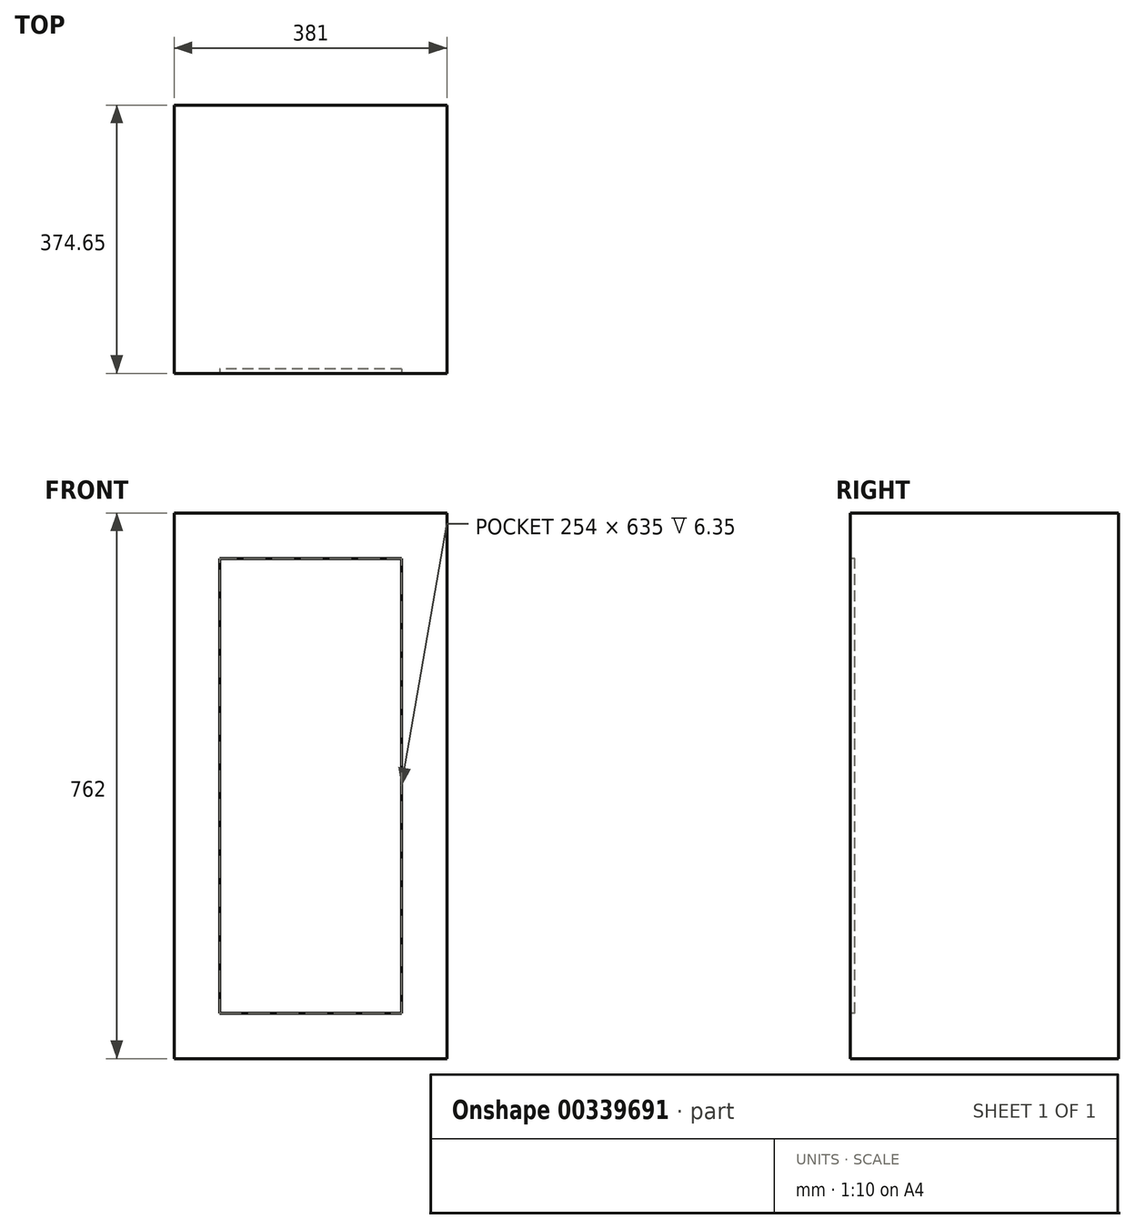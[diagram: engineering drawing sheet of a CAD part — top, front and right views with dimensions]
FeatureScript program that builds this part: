
annotation { "Feature Type Name" : "Feature", "Feature Type Description" : "" }
export const myFeature = defineFeature(function(context is Context, id is Id, definition is map)
    precondition{}
    {
        {
            var Q0;
            Q0=qCreatedBy(makeId("Front.planeOp"),FACE);
            var sketch = newSketch(context, id + "F0", { "sketchPlane" : qUnion([Q0])});
            skLineSegment(sketch, "E0.bottom", {"start": v(263.93, 0) * mm, "end": v(-117.07, 0) * mm});
            skLineSegment(sketch, "E0.top", {"start": v(263.93, 762) * mm, "end": v(-117.07, 762) * mm});
            skLineSegment(sketch, "E0.left", {"start": v(263.93, 0) * mm, "end": v(263.93, 762) * mm});
            skLineSegment(sketch, "E0.right", {"start": v(-117.07, 0) * mm, "end": v(-117.07, 762) * mm});
            skLineSegment(sketch, "E1.0", {"start": v(200.43, 698.5) * mm, "end": v(-53.57, 698.5) * mm});
            skLineSegment(sketch, "E1.1", {"start": v(200.43, 63.5) * mm, "end": v(200.43, 698.5) * mm});
            skLineSegment(sketch, "E1.2", {"start": v(200.43, 63.5) * mm, "end": v(-53.57, 63.5) * mm});
            skLineSegment(sketch, "E1.3", {"start": v(-53.57, 63.5) * mm, "end": v(-53.57, 698.5) * mm});
            skLineSegment(sketch, "E2.bottom", {"start": v(-117.07, 0) * mm, "end": v(263.93, 0) * mm});
            skLineSegment(sketch, "E3.bottom", {"start": v(-117.07, 762) * mm, "end": v(263.93, 762) * mm});
            skSolve(sketch);
        }
        {
            var Q0;
            Q0=makeQuery(id+"F0.imprint","IMPRINT",FACE,{"disambiguationData":[TD([[makeQuery(id+"F0.imprint","IMPRINT",EDGE,{"derivedFrom":sQuery(id+"F0.wireOp",EDGE,"E0.top")}),1.0]])]});
            var Q1;
            Q1=makeQuery(id+"F0.imprint","IMPRINT",FACE,{"disambiguationData":[TD([[makeQuery(id+"F0.imprint","IMPRINT",EDGE,{"derivedFrom":sQuery(id+"F0.wireOp",EDGE,"E1.0")}),1.0]])]});
            var Q2;
            Q2=makeQuery(id+"F0.imprint","IMPRINT",FACE,{"disambiguationData":[TD([[makeQuery(id+"F0.imprint","IMPRINT",EDGE,{"derivedFrom":sQuery(id+"F0.wireOp",EDGE,"E2.bottom")}),-1.0]])]});
            var Q3;
            Q3=makeQuery(id+"F0.imprint","IMPRINT",FACE,{"disambiguationData":[TD([[makeQuery(id+"F0.imprint","IMPRINT",EDGE,{"derivedFrom":sQuery(id+"F0.wireOp",EDGE,"E3.bottom")}),1.0]])]});
            var Q4;
            Q4=makeQuery(id+"F0.imprint","IMPRINT",FACE,{"disambiguationData":[TD([[makeQuery(id+"F0.imprint","IMPRINT",EDGE,{"derivedFrom":sQuery(id+"F0.wireOp",EDGE,"E0.left")}),1.0]])]});
            var Q5;
            Q5=makeQuery(id+"F0.imprint","IMPRINT",FACE,{"disambiguationData":[TD([[makeQuery(id+"F0.imprint","IMPRINT",EDGE,{"derivedFrom":sQuery(id+"F0.wireOp",EDGE,"E3.top")}),-1.0]])]});
            var Q6;
            Q6=makeQuery(id+"F0.imprint","IMPRINT",FACE,{"disambiguationData":[TD([[makeQuery(id+"F0.imprint","IMPRINT",EDGE,{"derivedFrom":sQuery(id+"F0.wireOp",EDGE,"E3.bottom")}),1.0]])]});
            extrude(context, id + "F1", {"entities" : qUnion([Q0, Q1, Q2, Q3, Q4, Q5, Q6]), "oppositeDirection" : true, "depth" : 374.65 * mm, "offsetDistance" : 25.4 * mm});
        }
        {
            var Q0;
            Q0=makeQuery(id+"F0.imprint","IMPRINT",FACE,{"disambiguationData":[TD([[makeQuery(id+"F0.imprint","IMPRINT",EDGE,{"derivedFrom":sQuery(id+"F0.wireOp",EDGE,"E1.0")}),1.0]])]});
            var Q1;
            Q1=makeQuery(id+"F0.imprint","IMPRINT",FACE,{"disambiguationData":[TD([[makeQuery(id+"F0.imprint","IMPRINT",EDGE,{"derivedFrom":sQuery(id+"F0.wireOp",EDGE,"E3.bottom")}),1.0]])]});
            extrude(context, id + "F2", {"entities" : qUnion([Q0, Q1]), "operationType" : NewBodyOperationType.REMOVE, "oppositeDirection" : true, "depth" : 6.35 * mm});
        }
    });
